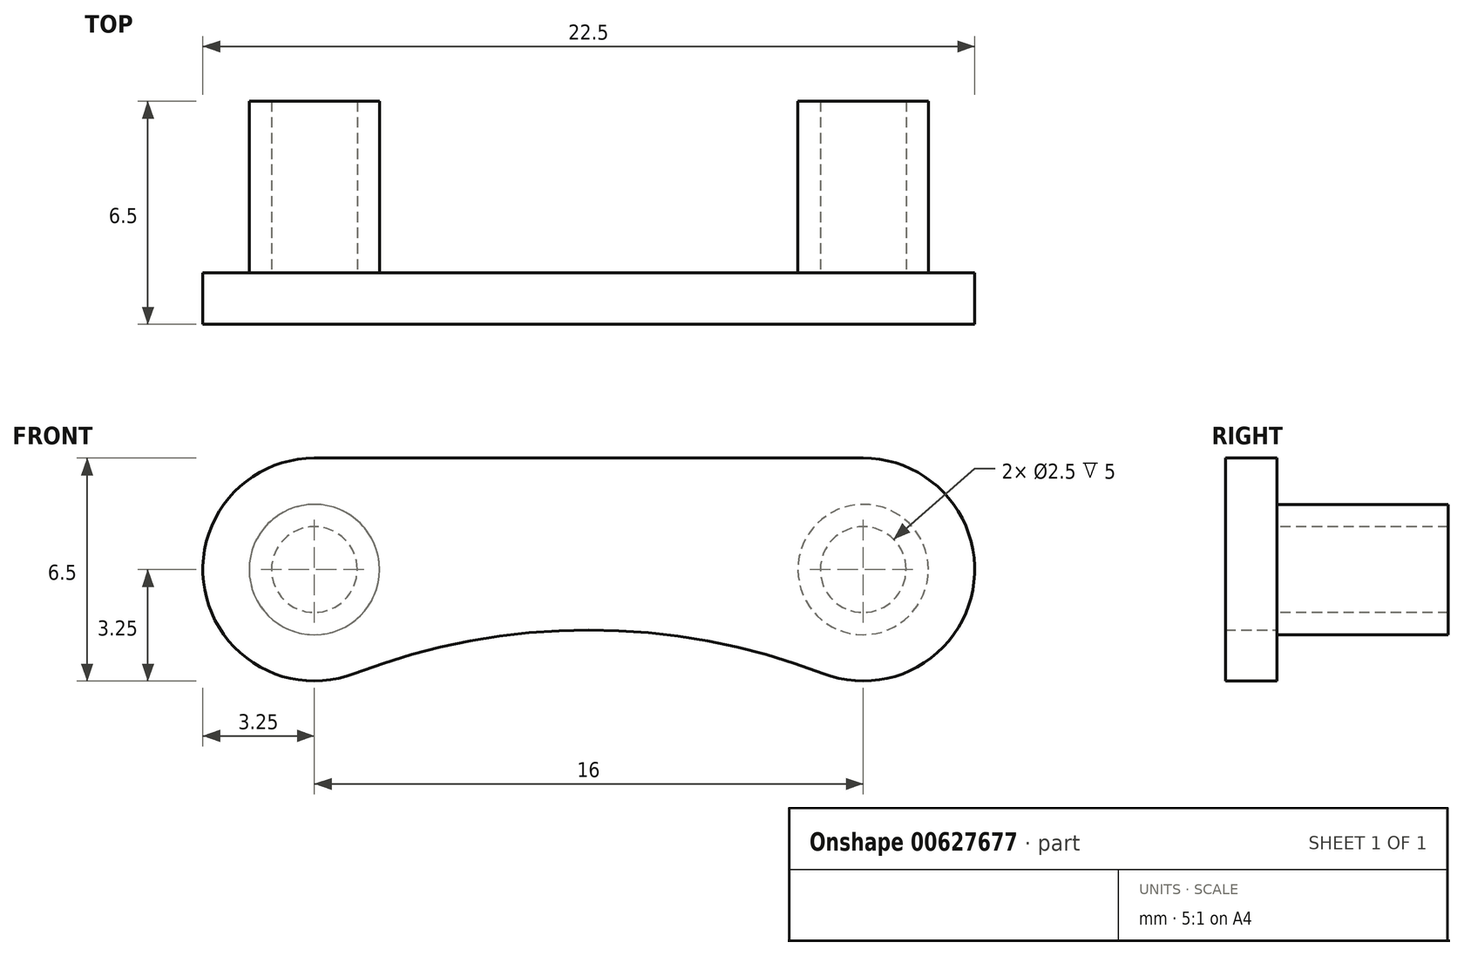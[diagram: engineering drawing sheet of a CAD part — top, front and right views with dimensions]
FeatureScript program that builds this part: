
annotation { "Feature Type Name" : "Feature", "Feature Type Description" : "" }
export const myFeature = defineFeature(function(context is Context, id is Id, definition is map)
    precondition{}
    {
        {
            var Q0;
            Q0=qCreatedBy(makeId("Front.planeOp"),FACE);
            var sketch = newSketch(context, id + "F0", { "sketchPlane" : qUnion([Q0])});
            skCircle(sketch, "E0", {"center": v(0, 0) * mm, "radius": 1.9 * mm, "construction": true});
            skCircle(sketch, "E1", {"center": v(16, 0) * mm, "radius": 1.9 * mm, "construction": true});
            skLineSegment(sketch, "E2", {"start": v(0, 0) * mm, "end": v(16, 0) * mm, "construction": true});
            skCircle(sketch, "E3", {"center": v(0, 0) * mm, "radius": 3.25 * mm});
            skCircle(sketch, "E4", {"center": v(16, 0) * mm, "radius": 3.25 * mm});
            skLineSegment(sketch, "E5", {"start": v(0, 3.25) * mm, "end": v(16, 3.25) * mm});
            skArc(sketch, "E6", {"start": v(14.83, -3.03) * mm, "mid": v(8, -1.76) * mm, "end": v(1.17, -3.03) * mm});
            skSolve(sketch);
        }
        {
            var Q0;
            Q0 = qSketchRegion(id + "F0", true);
            extrude(context, id + "F1", {"entities" : qUnion([Q0]), "depth" : 1.5 * mm, "offsetDistance" : 25 * mm});
        }
        {
            var Q0;
            Q0=makeQuery(id+"F1.opExtrude","CAP_FACE",FACE,{"disambiguationData":[OSD([sQuery(id+"F0.wireOp",EDGE,"E3"),sQuery(id+"F0.wireOp",EDGE,"E4"),sQuery(id+"F0.wireOp",EDGE,"E5"),sQuery(id+"F0.wireOp",EDGE,"E6")])],"isStart":true});
            var sketch = newSketch(context, id + "F2", { "sketchPlane" : qUnion([Q0])});
            skCircle(sketch, "E7.0", {"center": v(-16, 0) * mm, "radius": 1.9 * mm, "construction": true});
            skCircle(sketch, "E7.1", {"center": v(0, 0) * mm, "radius": 1.9 * mm, "construction": true});
            skCircle(sketch, "E8", {"center": v(-16, 0) * mm, "radius": 1.25 * mm});
            skCircle(sketch, "E9", {"center": v(0, 0) * mm, "radius": 1.25 * mm});
            skCircle(sketch, "E10.0", {"center": v(-16, 0) * mm, "radius": 1.9 * mm});
            skCircle(sketch, "E11.0", {"center": v(0, 0) * mm, "radius": 1.9 * mm});
            skSolve(sketch);
        }
        {
            var Q0;
            Q0 = qSketchRegion(id + "F2", true);
            extrude(context, id + "F3", {"entities" : qUnion([Q0]), "operationType" : NewBodyOperationType.ADD, "depth" : 5 * mm, "offsetDistance" : 25 * mm});
        }
    });
